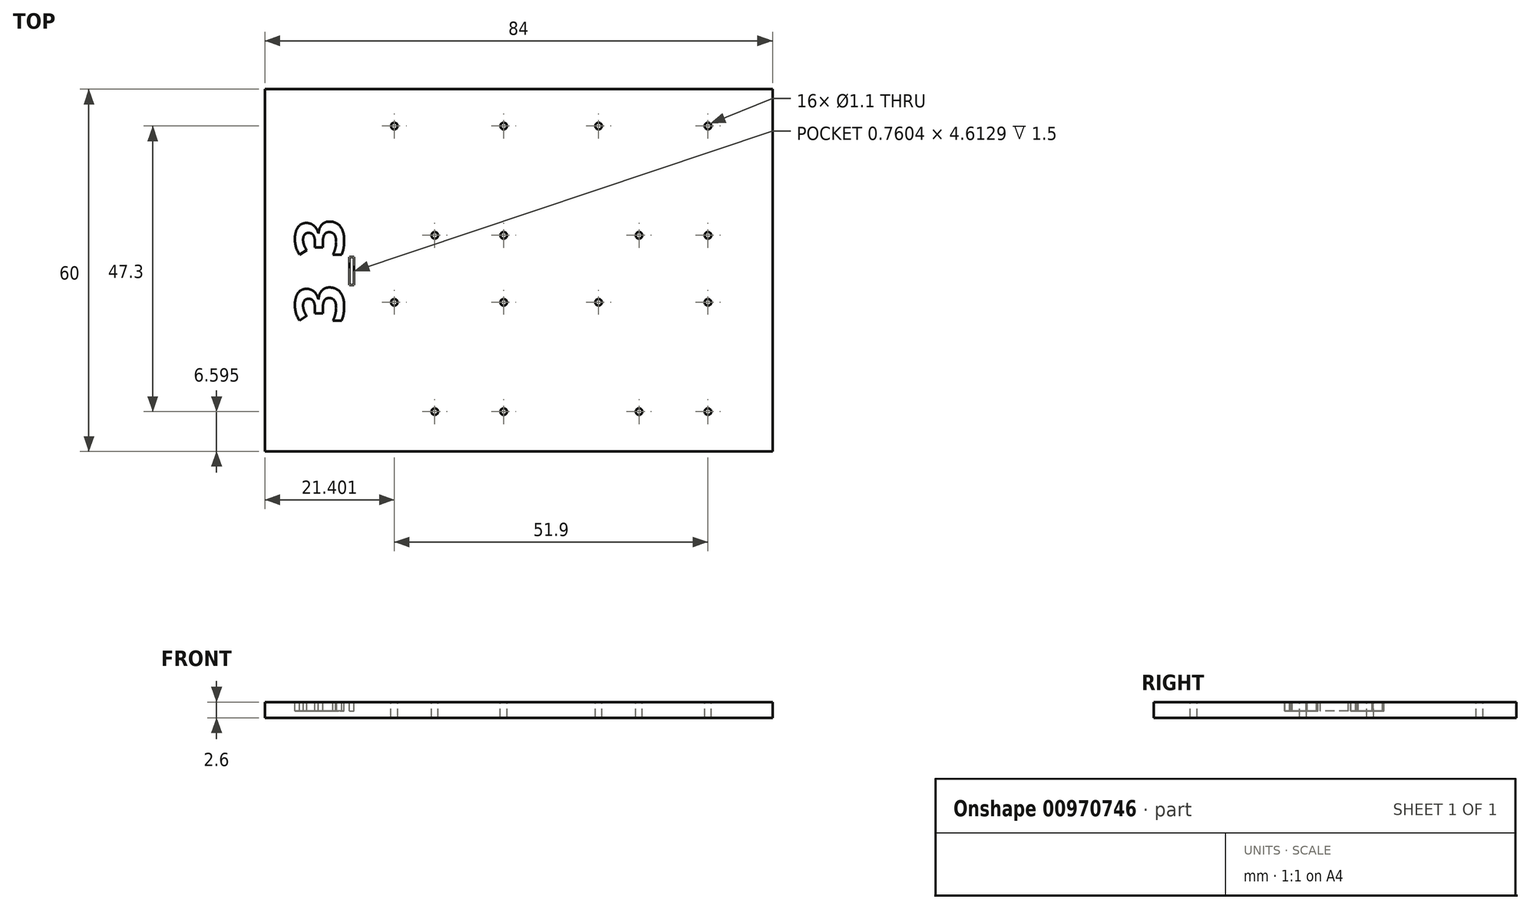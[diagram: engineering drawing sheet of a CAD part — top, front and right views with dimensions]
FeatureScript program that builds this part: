
annotation { "Feature Type Name" : "Feature", "Feature Type Description" : "" }
export const myFeature = defineFeature(function(context is Context, id is Id, definition is map)
    precondition{}
    {
        {
            var Q0;
            Q0=qCreatedBy(makeId("Top.planeOp"),FACE);
            var sketch = newSketch(context, id + "F0", { "sketchPlane" : qUnion([Q0])});
            skLineSegment(sketch, "E0.bottom", {"start": v(-43.16, 38.34) * mm, "end": v(40.84, 38.34) * mm});
            skLineSegment(sketch, "E0.top", {"start": v(-43.16, -21.66) * mm, "end": v(40.84, -21.66) * mm});
            skLineSegment(sketch, "E0.left", {"start": v(-43.16, 38.34) * mm, "end": v(-43.16, -21.66) * mm});
            skLineSegment(sketch, "E0.right", {"start": v(40.84, 38.34) * mm, "end": v(40.84, -21.66) * mm});
            skSolve(sketch);
        }
        {
            var Q0;
            Q0=makeQuery(id+"F0.imprint","IMPRINT",FACE,{"disambiguationData":[TD([[makeQuery(id+"F0.imprint","IMPRINT",EDGE,{"derivedFrom":sQuery(id+"F0.wireOp",EDGE,"E0.bottom")}),-1.0]])]});
            extrude(context, id + "F1", {"entities" : qUnion([Q0]), "depth" : 2.6 * mm, "offsetDistance" : 25 * mm});
        }
        {
            var Q0;
            Q0=makeQuery(id+"F1.opExtrude","CAP_FACE",FACE,{"disambiguationData":[OSD([sQuery(id+"F0.wireOp",EDGE,"E0.bottom"),sQuery(id+"F0.wireOp",EDGE,"E0.top"),sQuery(id+"F0.wireOp",EDGE,"E0.left"),sQuery(id+"F0.wireOp",EDGE,"E0.right")])],"isStart":false});
            var sketch = newSketch(context, id + "F2", { "sketchPlane" : qUnion([Q0])});
            skText(sketch, "E1", { "text": "3_3", "fontName": "OpenSans-Bold.ttf"});
            const initialGuessF2  = {"E1": [-0.03016, -0.00041, 0, 1, 0.008]};
            skSetInitialGuess(sketch, initialGuessF2);
            skSolve(sketch);
        }
        {
            var Q0;
            Q0=qSketchRegion(id+"F2",true);
            extrude(context, id + "F3", {"entities" : qUnion([Q0]), "operationType" : NewBodyOperationType.REMOVE, "oppositeDirection" : true, "depth" : 1.5 * mm, "offsetDistance" : 25 * mm});
        }
        {
            var Q0;
            {var subQ0=sQuery(id+"F0.wireOp",EDGE,"E0.left");var subQ1=sQuery(id+"F0.wireOp",EDGE,"E0.bottom");var subQ2=sQuery(id+"F0.wireOp",EDGE,"E0.right");var subQ3=sQuery(id+"F0.wireOp",EDGE,"E0.top");Q0=makeQuery(id+"F3.boolean.opBoolean","SPLIT",FACE,{"disambiguationData":[TD([makeQuery(id+"F1.opExtrude","SWEPT_FACE",FACE,{"disambiguationData":[OSD([subQ1])]})])],"derivedFrom":makeQuery(id+"F1.opExtrude","CAP_FACE",FACE,{"disambiguationData":[OSD([subQ1,subQ3,subQ0,subQ2])],"isStart":false})});}
            var sketch = newSketch(context, id + "F4", { "sketchPlane" : qUnion([Q0])});
            skLineSegment(sketch, "E2.bottom", {"start": v(-27.16, 37.34) * mm, "end": v(1.64, 37.34) * mm});
            skLineSegment(sketch, "E2.top", {"start": v(-27.16, 8.54) * mm, "end": v(1.64, 8.54) * mm});
            skLineSegment(sketch, "E2.left", {"start": v(-27.16, 37.34) * mm, "end": v(-27.16, 8.54) * mm});
            skLineSegment(sketch, "E2.right", {"start": v(1.64, 37.34) * mm, "end": v(1.64, 8.54) * mm});
            skLineSegment(sketch, "E3.bottom", {"start": v(-27.16, 8.14) * mm, "end": v(1.64, 8.14) * mm});
            skLineSegment(sketch, "E3.top", {"start": v(-27.16, -20.66) * mm, "end": v(1.64, -20.66) * mm});
            skLineSegment(sketch, "E3.left", {"start": v(-27.16, 8.14) * mm, "end": v(-27.16, -20.66) * mm});
            skLineSegment(sketch, "E3.right", {"start": v(1.64, 8.14) * mm, "end": v(1.64, -20.66) * mm});
            skCircle(sketch, "E4", {"center": v(-21.76, 32.24) * mm, "radius": 0.55 * mm});
            skCircle(sketch, "E5", {"center": v(-3.66, 32.24) * mm, "radius": 0.55 * mm});
            skCircle(sketch, "E6", {"center": v(-15.06, 14.14) * mm, "radius": 0.55 * mm});
            skCircle(sketch, "E7", {"center": v(-3.66, 14.14) * mm, "radius": 0.55 * mm});
            skCircle(sketch, "E8", {"center": v(-21.76, 3.04) * mm, "radius": 0.55 * mm});
            skCircle(sketch, "E9", {"center": v(-3.66, 3.04) * mm, "radius": 0.55 * mm});
            skCircle(sketch, "E10", {"center": v(-15.06, -15.06) * mm, "radius": 0.55 * mm});
            skCircle(sketch, "E11", {"center": v(-3.66, -15.06) * mm, "radius": 0.55 * mm});
            skLineSegment(sketch, "E12.bottom", {"start": v(6.64, 37.34) * mm, "end": v(35.44, 37.34) * mm});
            skLineSegment(sketch, "E12.top", {"start": v(6.64, 8.54) * mm, "end": v(35.44, 8.54) * mm});
            skLineSegment(sketch, "E12.left", {"start": v(6.64, 37.34) * mm, "end": v(6.64, 8.54) * mm});
            skLineSegment(sketch, "E12.right", {"start": v(35.44, 37.34) * mm, "end": v(35.44, 8.54) * mm});
            skLineSegment(sketch, "E13.bottom", {"start": v(6.64, 8.14) * mm, "end": v(35.44, 8.14) * mm});
            skLineSegment(sketch, "E13.top", {"start": v(6.64, -20.66) * mm, "end": v(35.44, -20.66) * mm});
            skLineSegment(sketch, "E13.left", {"start": v(6.64, 8.14) * mm, "end": v(6.64, -20.66) * mm});
            skLineSegment(sketch, "E13.right", {"start": v(35.44, 8.14) * mm, "end": v(35.44, -20.66) * mm});
            skCircle(sketch, "E14", {"center": v(12.04, 32.24) * mm, "radius": 0.55 * mm});
            skCircle(sketch, "E15", {"center": v(30.14, 32.24) * mm, "radius": 0.55 * mm});
            skCircle(sketch, "E16", {"center": v(18.74, 14.14) * mm, "radius": 0.55 * mm});
            skCircle(sketch, "E17", {"center": v(30.14, 14.14) * mm, "radius": 0.55 * mm});
            skCircle(sketch, "E18", {"center": v(12.04, 3.04) * mm, "radius": 0.55 * mm});
            skCircle(sketch, "E19", {"center": v(30.14, 3.04) * mm, "radius": 0.55 * mm});
            skCircle(sketch, "E20", {"center": v(18.74, -15.06) * mm, "radius": 0.55 * mm});
            skCircle(sketch, "E21", {"center": v(30.14, -15.06) * mm, "radius": 0.55 * mm});
            skSolve(sketch);
        }
        {
            var Q0;
            Q0=makeQuery(id+"F4.imprint","IMPRINT",FACE,{"disambiguationData":[TD([[makeQuery(id+"F4.imprint","IMPRINT",EDGE,{"derivedFrom":sQuery(id+"F4.wireOp",EDGE,"E4")}),1.0]])]});
            var Q1;
            Q1=makeQuery(id+"F4.imprint","IMPRINT",FACE,{"disambiguationData":[TD([[makeQuery(id+"F4.imprint","IMPRINT",EDGE,{"derivedFrom":sQuery(id+"F4.wireOp",EDGE,"E5")}),1.0]])]});
            var Q2;
            Q2=makeQuery(id+"F4.imprint","IMPRINT",FACE,{"disambiguationData":[TD([[makeQuery(id+"F4.imprint","IMPRINT",EDGE,{"derivedFrom":sQuery(id+"F4.wireOp",EDGE,"E7")}),1.0]])]});
            var Q3;
            Q3=makeQuery(id+"F4.imprint","IMPRINT",FACE,{"disambiguationData":[TD([[makeQuery(id+"F4.imprint","IMPRINT",EDGE,{"derivedFrom":sQuery(id+"F4.wireOp",EDGE,"E6")}),1.0]])]});
            var Q4;
            Q4=makeQuery(id+"F4.imprint","IMPRINT",FACE,{"disambiguationData":[TD([[makeQuery(id+"F4.imprint","IMPRINT",EDGE,{"derivedFrom":sQuery(id+"F4.wireOp",EDGE,"E16")}),1.0]])]});
            var Q5;
            Q5=makeQuery(id+"F4.imprint","IMPRINT",FACE,{"disambiguationData":[TD([[makeQuery(id+"F4.imprint","IMPRINT",EDGE,{"derivedFrom":sQuery(id+"F4.wireOp",EDGE,"E14")}),1.0]])]});
            var Q6;
            Q6=makeQuery(id+"F4.imprint","IMPRINT",FACE,{"disambiguationData":[TD([[makeQuery(id+"F4.imprint","IMPRINT",EDGE,{"derivedFrom":sQuery(id+"F4.wireOp",EDGE,"E15")}),1.0]])]});
            var Q7;
            Q7=makeQuery(id+"F4.imprint","IMPRINT",FACE,{"disambiguationData":[TD([[makeQuery(id+"F4.imprint","IMPRINT",EDGE,{"derivedFrom":sQuery(id+"F4.wireOp",EDGE,"E17")}),1.0]])]});
            var Q8;
            Q8=makeQuery(id+"F4.imprint","IMPRINT",FACE,{"disambiguationData":[TD([[makeQuery(id+"F4.imprint","IMPRINT",EDGE,{"derivedFrom":sQuery(id+"F4.wireOp",EDGE,"E19")}),1.0]])]});
            var Q9;
            Q9=makeQuery(id+"F4.imprint","IMPRINT",FACE,{"disambiguationData":[TD([[makeQuery(id+"F4.imprint","IMPRINT",EDGE,{"derivedFrom":sQuery(id+"F4.wireOp",EDGE,"E18")}),1.0]])]});
            var Q10;
            Q10=makeQuery(id+"F4.imprint","IMPRINT",FACE,{"disambiguationData":[TD([[makeQuery(id+"F4.imprint","IMPRINT",EDGE,{"derivedFrom":sQuery(id+"F4.wireOp",EDGE,"E9")}),1.0]])]});
            var Q11;
            Q11=makeQuery(id+"F4.imprint","IMPRINT",FACE,{"disambiguationData":[TD([[makeQuery(id+"F4.imprint","IMPRINT",EDGE,{"derivedFrom":sQuery(id+"F4.wireOp",EDGE,"E8")}),1.0]])]});
            var Q12;
            Q12=makeQuery(id+"F4.imprint","IMPRINT",FACE,{"disambiguationData":[TD([[makeQuery(id+"F4.imprint","IMPRINT",EDGE,{"derivedFrom":sQuery(id+"F4.wireOp",EDGE,"E10")}),1.0]])]});
            var Q13;
            Q13=makeQuery(id+"F4.imprint","IMPRINT",FACE,{"disambiguationData":[TD([[makeQuery(id+"F4.imprint","IMPRINT",EDGE,{"derivedFrom":sQuery(id+"F4.wireOp",EDGE,"E11")}),1.0]])]});
            var Q14;
            Q14=makeQuery(id+"F4.imprint","IMPRINT",FACE,{"disambiguationData":[TD([[makeQuery(id+"F4.imprint","IMPRINT",EDGE,{"derivedFrom":sQuery(id+"F4.wireOp",EDGE,"E21")}),1.0]])]});
            var Q15;
            Q15=makeQuery(id+"F4.imprint","IMPRINT",FACE,{"disambiguationData":[TD([[makeQuery(id+"F4.imprint","IMPRINT",EDGE,{"derivedFrom":sQuery(id+"F4.wireOp",EDGE,"E20")}),1.0]])]});
            extrude(context, id + "F5", {"entities" : qUnion([Q0, Q1, Q2, Q3, Q4, Q5, Q6, Q7, Q8, Q9, Q10, Q11, Q12, Q13, Q14, Q15]), "operationType" : NewBodyOperationType.REMOVE, "endBound" : BoundingType.UP_TO_NEXT, "oppositeDirection" : true, "depth" : 25 * mm, "offsetDistance" : 25 * mm});
        }
    });
